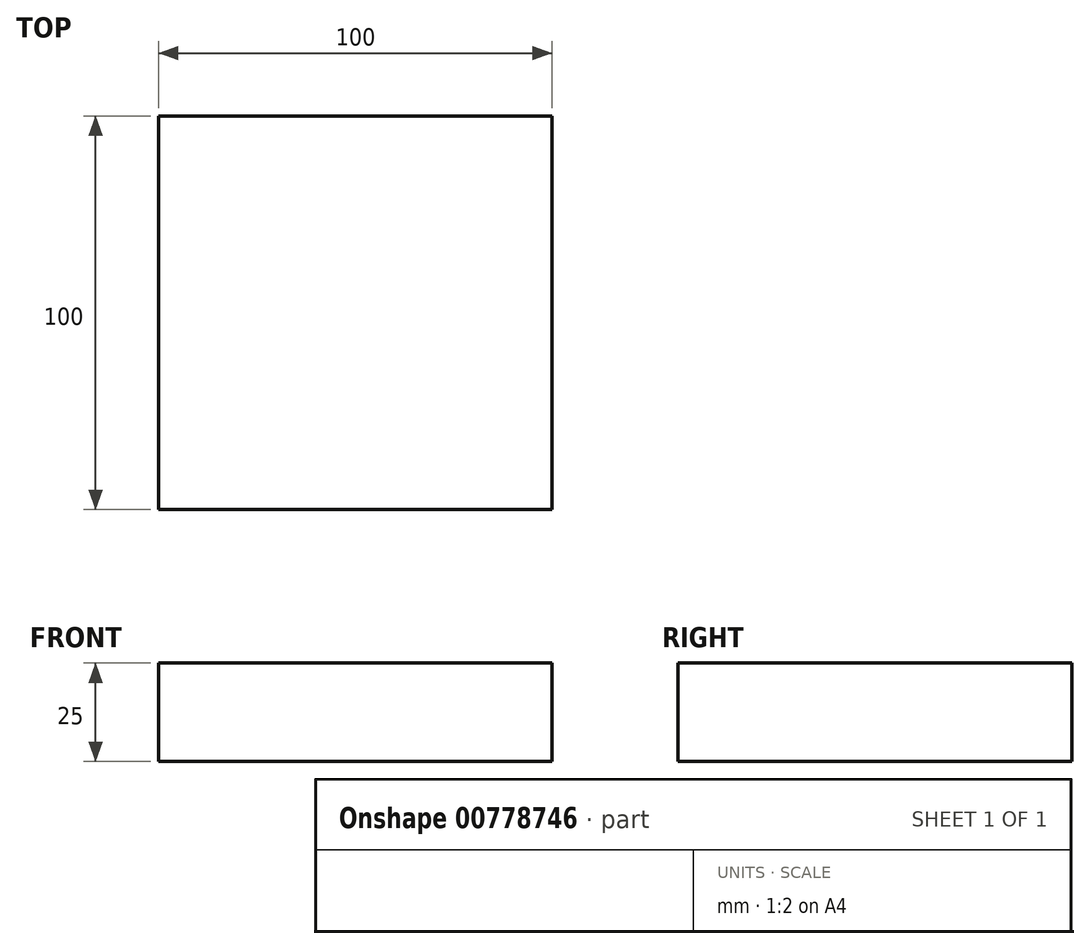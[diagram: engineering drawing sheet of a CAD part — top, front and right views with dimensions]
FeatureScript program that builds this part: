
annotation { "Feature Type Name" : "Feature", "Feature Type Description" : "" }
export const myFeature = defineFeature(function(context is Context, id is Id, definition is map)
    precondition{}
    {
        {
            var Q0;
            Q0=qCreatedBy(makeId("Top.planeOp"),FACE);
            var sketch = newSketch(context, id + "F0", { "sketchPlane" : qUnion([Q0])});
            skLineSegment(sketch, "E0.bottom", {"start": v(0, 0) * mm, "end": v(100, 0) * mm});
            skLineSegment(sketch, "E0.top", {"start": v(0, -100) * mm, "end": v(100, -100) * mm});
            skLineSegment(sketch, "E0.left", {"start": v(0, 0) * mm, "end": v(0, -100) * mm});
            skLineSegment(sketch, "E0.right", {"start": v(100, 0) * mm, "end": v(100, -100) * mm});
            skSolve(sketch);
        }
        {
            var Q0;
            Q0=makeQuery(id+"F0.imprint","IMPRINT",FACE,{"disambiguationData":[TD([[makeQuery(id+"F0.imprint","IMPRINT",EDGE,{"derivedFrom":sQuery(id+"F0.wireOp",EDGE,"E0.bottom")}),-1.0]])]});
            extrude(context, id + "F1", {"entities" : qUnion([Q0]), "depth" : 25 * mm, "offsetDistance" : 25 * mm});
        }
    });
